# Revit family: Gira_542000
name_source: partatom
category: Elektroinstallationen
revit_build: Autodesk Revit 2017 (Build: 20160225_1515(x64)
units: mm (PartAtom-declared; Revit-internal decimal feet)

## family parameters
Basisbauteil = Fläche
Beim Laden mit Abzugskörper schneiden = Nein
Bemaßung runder Anschluss = Durchmesser verwenden
Beschriftungsausrichtung beibehalten = Nein
Gemeinsam genutzt = Nein
Raumberechnungspunkt = Nein
Teiletyp = Normal

## types (1)
- Gira_542000
    Anzahl der Ausgänge = 1
    BIM = https://media.stage.bim.site
    Beschreibung = eNet Funk Dimmaktor 1fach Mini 20 - 250 W VA  Merkmale: Mit eNet Server einstellbar:: - Vollverschlüsselte Funkübertragung (AES-CCM) ab eNet Server Software Version 2.0. - Bediensperren. - Update der Gerätesoftware. - Der eNet Funk Dimmaktor ermöglicht das Schalten und Dimmen von verschiedenen elektrischen Lasten. - Schalten und Dimmen von Glühlampen, HV-Halogenlampen, elektronischen Trafos für Halogen- oder LED-Lampen, dimmbaren induktiven Trafos für Halogen- oder LED-Lampen, HV-LED- oder Kompaktleuchtstofflampen. - Lampenschonendes Einschalten. - Einschalt- und Minimalhelligkeit für jeden Ausgang speicherbar. - Szenenbetrieb. - Statusanzeige mit LED. - Statusrückmeldung an eNet Funksensoren. - Kurzschluss- und Übertemperaturschutz. - Automatische oder manuelle Einstellung des Dimmverfahrens. Mit eNet Server einstellbar:: - Maximale Helligkeit. - Dimmverfahren. - Dimmgeschwindigkeit. - Nachlaufzeit. - Ein- bzw. Ausschaltverzögerung. - Auf- bzw. Abdimmrampe. - Abschaltvorwarnung. - Dauer-Ein, Dauer-Aus. - Hotelfunktion. - Lichtregelung. - Repeaterfunktion. - Lokalisierung des Geräts.  Hinweise : - Montage in Gerätedose, Aufputz-Gehäuse oder im Einbauadapter.
    Datenblatt = https://katalog.gira.de
    GTIN = 4010337774143
    HAN = 542000
    Hersteller = Gira
    Produktseite = http://katalog.gira.de
    Typname = Funk Dimmaktor 1f Mini 20 - 250 VA Gira eNet
    URL = https://www.gira.de
    Vorgabe-Ansicht = 1219 mm

## geometry (parser evidence)
native form markers: Sweep x2
no freeform markers — native parametric forms only
